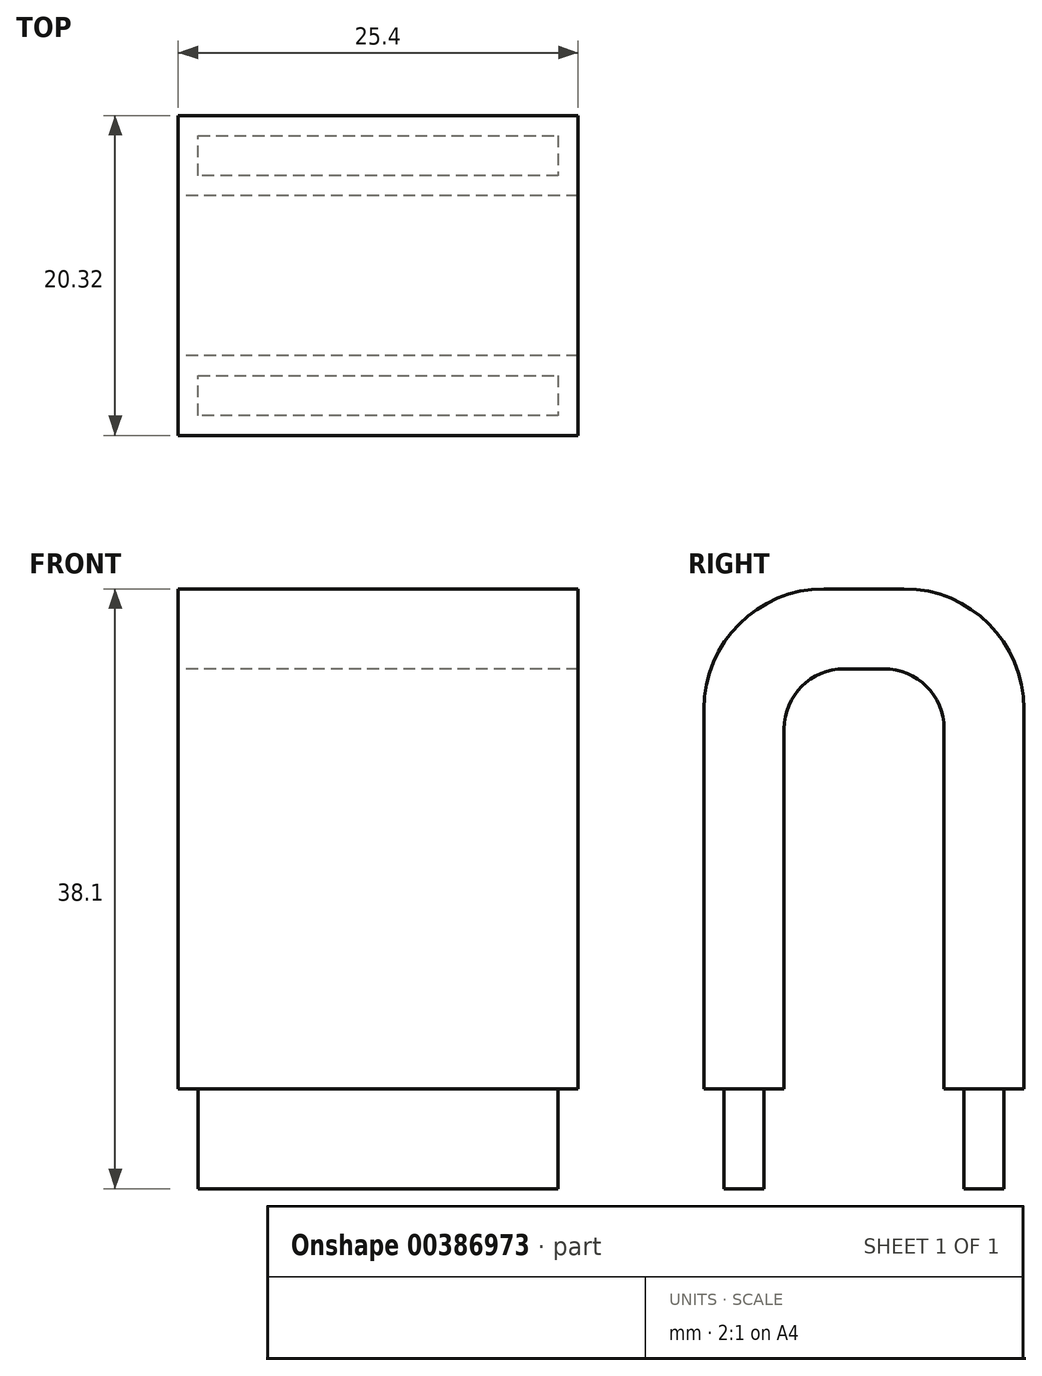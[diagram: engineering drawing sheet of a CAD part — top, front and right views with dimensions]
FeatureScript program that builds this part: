
annotation { "Feature Type Name" : "Feature", "Feature Type Description" : "" }
export const myFeature = defineFeature(function(context is Context, id is Id, definition is map)
    precondition{}
    {
        {
            var Q0;
            Q0=qCreatedBy(makeId("Right.planeOp"),FACE);
            var sketch = newSketch(context, id + "F0", { "sketchPlane" : qUnion([Q0])});
            skLineSegment(sketch, "E0", {"start": v(0, 0) * mm, "end": v(0, 31.75) * mm});
            skLineSegment(sketch, "E1", {"start": v(-10.16, 0) * mm, "end": v(-10.16, 24.13) * mm});
            skLineSegment(sketch, "E2", {"start": v(-2.54, 31.75) * mm, "end": v(2.54, 31.75) * mm});
            skLineSegment(sketch, "E3", {"start": v(10.16, 24.13) * mm, "end": v(10.16, 0) * mm});
            skLineSegment(sketch, "E4.0", {"start": v(5.08, 22.86) * mm, "end": v(5.08, 0) * mm});
            skLineSegment(sketch, "E4.1", {"start": v(-1.27, 26.67) * mm, "end": v(1.27, 26.67) * mm});
            skLineSegment(sketch, "E4.2", {"start": v(-5.08, 0) * mm, "end": v(-5.08, 22.86) * mm});
            skPoint(sketch, "E5.visualSharp", {"position": v(-5.08, 26.67) * mm});
            skArc(sketch, "E5.filletArc", {"start": v(-1.27, 26.67) * mm, "mid": v(-3.96, 25.55) * mm, "end": v(-5.08, 22.86) * mm});
            skPoint(sketch, "E6.visualSharp", {"position": v(5.08, 26.67) * mm});
            skArc(sketch, "E6.filletArc", {"start": v(5.08, 22.86) * mm, "mid": v(3.96, 25.55) * mm, "end": v(1.27, 26.67) * mm});
            skPoint(sketch, "E7.visualSharp", {"position": v(-10.16, 31.75) * mm});
            skArc(sketch, "E7.filletArc", {"start": v(-2.54, 31.75) * mm, "mid": v(-7.93, 29.52) * mm, "end": v(-10.16, 24.13) * mm});
            skPoint(sketch, "E8.visualSharp", {"position": v(10.16, 31.75) * mm});
            skArc(sketch, "E8.filletArc", {"start": v(10.16, 24.13) * mm, "mid": v(7.93, 29.52) * mm, "end": v(2.54, 31.75) * mm});
            skPoint(sketch, "E9.orphan", {"position": v(10.16, 1.3) * mm});
            skLineSegment(sketch, "E10", {"start": v(-10.16, 0) * mm, "end": v(-5.08, 0) * mm});
            skLineSegment(sketch, "E11", {"start": v(5.08, 0) * mm, "end": v(10.16, 0) * mm});
            skLineSegment(sketch, "E12", {"start": v(-5.08, 0) * mm, "end": v(5.08, 0) * mm});
            skSolve(sketch);
        }
        {
            var Q0;
            Q0=makeQuery(id+"F0.imprint","IMPRINT",FACE,{"disambiguationData":[TD([[makeQuery(id+"F0.imprint","IMPRINT",EDGE,{"derivedFrom":sQuery(id+"F0.wireOp",EDGE,"E3")}),-1.0]])]});
            var Q1;
            Q1=makeQuery(id+"F0.imprint","IMPRINT",FACE,{"disambiguationData":[TD([[makeQuery(id+"F0.imprint","IMPRINT",EDGE,{"derivedFrom":sQuery(id+"F0.wireOp",EDGE,"E1")}),-1.0]])]});
            extrude(context, id + "F1", {"entities" : qUnion([Q0, Q1]), "endBound" : BoundingType.SYMMETRIC, "depth" : 25.4 * mm});
        }
        {
            var Q0;
            Q0=makeQuery(id+"F1.opExtrude","SWEPT_FACE",FACE,{"disambiguationData":[OSD([sQuery(id+"F0.wireOp",EDGE,"E10")])]});
            var sketch = newSketch(context, id + "F2", { "sketchPlane" : qUnion([Q0])});
            skLineSegment(sketch, "E13.0.0", {"start": v(-12.7, 10.16) * mm, "end": v(-12.7, 5.08) * mm});
            skLineSegment(sketch, "E13.0.1", {"start": v(-12.7, 5.08) * mm, "end": v(12.7, 5.08) * mm});
            skLineSegment(sketch, "E13.0.2", {"start": v(12.7, 5.08) * mm, "end": v(12.7, 10.16) * mm});
            skLineSegment(sketch, "E13.0.3", {"start": v(12.7, 10.16) * mm, "end": v(-12.7, 10.16) * mm});
            skLineSegment(sketch, "E14.0.0", {"start": v(-12.7, -5.08) * mm, "end": v(-12.7, -10.16) * mm});
            skLineSegment(sketch, "E14.0.1", {"start": v(-12.7, -10.16) * mm, "end": v(12.7, -10.16) * mm});
            skLineSegment(sketch, "E14.0.2", {"start": v(12.7, -10.16) * mm, "end": v(12.7, -5.08) * mm});
            skLineSegment(sketch, "E14.0.3", {"start": v(12.7, -5.08) * mm, "end": v(-12.7, -5.08) * mm});
            skLineSegment(sketch, "E15.0", {"start": v(11.43, 8.9) * mm, "end": v(-11.43, 8.9) * mm});
            skLineSegment(sketch, "E16.0", {"start": v(-11.43, 8.9) * mm, "end": v(-11.43, 6.35) * mm});
            skLineSegment(sketch, "E17.0", {"start": v(11.43, 6.35) * mm, "end": v(11.43, 8.9) * mm});
            skLineSegment(sketch, "E18.0", {"start": v(-11.43, 6.35) * mm, "end": v(11.43, 6.35) * mm});
            skLineSegment(sketch, "E19.0", {"start": v(11.43, -6.35) * mm, "end": v(-11.43, -6.35) * mm});
            skLineSegment(sketch, "E20.0", {"start": v(-11.43, -8.9) * mm, "end": v(11.43, -8.9) * mm});
            skLineSegment(sketch, "E21.0", {"start": v(11.43, -8.9) * mm, "end": v(11.43, -6.35) * mm});
            skLineSegment(sketch, "E22.0", {"start": v(-11.43, -6.35) * mm, "end": v(-11.43, -8.9) * mm});
            skSolve(sketch);
        }
        {
            var Q0;
            Q0=makeQuery(id+"F2.imprint","IMPRINT",FACE,{"disambiguationData":[TD([[makeQuery(id+"F2.imprint","IMPRINT",EDGE,{"derivedFrom":sQuery(id+"F2.wireOp",EDGE,"E15.0")}),1.0]])]});
            var Q1;
            Q1=makeQuery(id+"F2.imprint","IMPRINT",FACE,{"disambiguationData":[TD([[makeQuery(id+"F2.imprint","IMPRINT",EDGE,{"derivedFrom":sQuery(id+"F2.wireOp",EDGE,"E19.0")}),1.0]])]});
            extrude(context, id + "F3", {"entities" : qUnion([Q0, Q1]), "operationType" : NewBodyOperationType.ADD, "depth" : 6.35 * mm});
        }
    });
